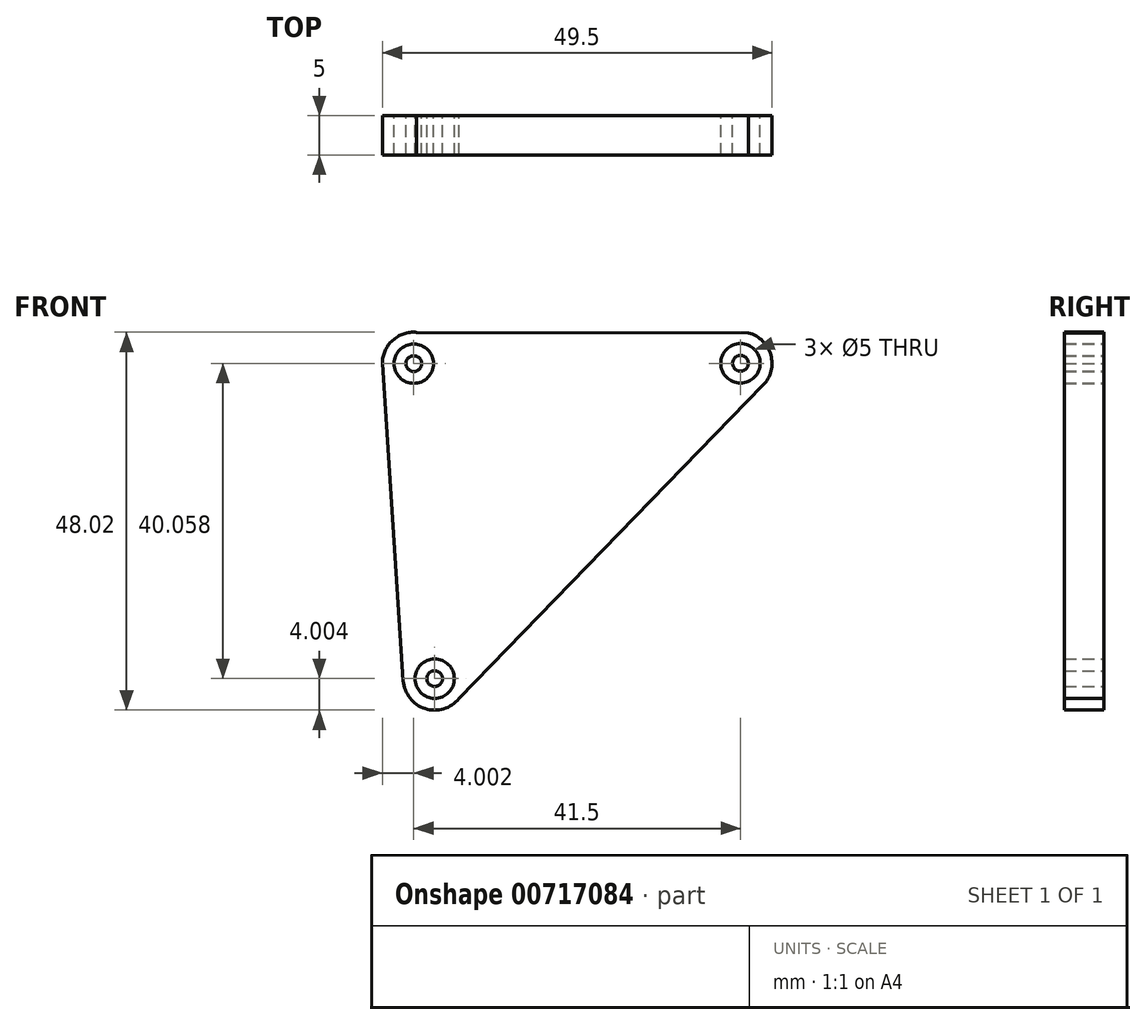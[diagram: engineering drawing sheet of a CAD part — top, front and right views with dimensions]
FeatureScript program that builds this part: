
annotation { "Feature Type Name" : "Feature", "Feature Type Description" : "" }
export const myFeature = defineFeature(function(context is Context, id is Id, definition is map)
    precondition{}
    {
        {
            var Q0;
            Q0=qCreatedBy(makeId("Front.planeOp"),FACE);
            var sketch = newSketch(context, id + "F0", { "sketchPlane" : qUnion([Q0])});
            skCircle(sketch, "E0", {"center": v(-13.99, 13.26) * mm, "radius": 2.5 * mm});
            skCircle(sketch, "E1", {"center": v(27.51, 13.3) * mm, "radius": 2.5 * mm});
            skCircle(sketch, "E2", {"center": v(-11.33, -26.76) * mm, "radius": 2.5 * mm});
            skArc(sketch, "E3", {"start": v(-13.65, 17.24) * mm, "mid": v(-16.9, 16) * mm, "end": v(-17.95, 12.7) * mm});
            skArc(sketch, "E4", {"start": v(30.38, 10.52) * mm, "mid": v(30.96, 15.32) * mm, "end": v(26.48, 17.17) * mm});
            skArc(sketch, "E5", {"start": v(-15.32, -27.02) * mm, "mid": v(-12.55, -30.57) * mm, "end": v(-8.24, -29.29) * mm});
            skLineSegment(sketch, "E6", {"start": v(-13.65, 17.24) * mm, "end": v(28.56, 17.16) * mm});
            skLineSegment(sketch, "E7", {"start": v(-17.99, 13.29) * mm, "end": v(-15.32, -27.02) * mm});
            skLineSegment(sketch, "E8", {"start": v(-8.24, -29.29) * mm, "end": v(30.38, 10.52) * mm});
            skCircle(sketch, "E9", {"center": v(-13.99, 13.26) * mm, "radius": 1 * mm});
            skCircle(sketch, "E10", {"center": v(-11.33, -26.76) * mm, "radius": 1 * mm});
            skCircle(sketch, "E11", {"center": v(27.51, 13.3) * mm, "radius": 1 * mm});
            skSolve(sketch);
        }
        {
            var Q0;
            Q0=makeQuery(id+"F0.imprint","IMPRINT",FACE,{"disambiguationData":[TD([[makeQuery(id+"F0.imprint","IMPRINT",EDGE,{"derivedFrom":sQuery(id+"F0.wireOp",EDGE,"E0")}),-1.0]])]});
            extrude(context, id + "F1", {"entities" : qUnion([Q0]), "depth" : 5 * mm, "offsetDistance" : 25.4 * mm});
        }
        {
            var Q0;
            Q0=makeQuery(id+"F0.imprint","IMPRINT",FACE,{"disambiguationData":[TD([[makeQuery(id+"F0.imprint","IMPRINT",EDGE,{"derivedFrom":sQuery(id+"F0.wireOp",EDGE,"E9")}),1.0]])]});
            var Q1;
            Q1=makeQuery(id+"F0.imprint","IMPRINT",FACE,{"disambiguationData":[TD([[makeQuery(id+"F0.imprint","IMPRINT",EDGE,{"derivedFrom":sQuery(id+"F0.wireOp",EDGE,"E11")}),1.0]])]});
            var Q2;
            Q2=makeQuery(id+"F0.imprint","IMPRINT",FACE,{"disambiguationData":[TD([[makeQuery(id+"F0.imprint","IMPRINT",EDGE,{"derivedFrom":sQuery(id+"F0.wireOp",EDGE,"E10")}),1.0]])]});
            extrude(context, id + "F2", {"entities" : qUnion([Q0, Q1, Q2]), "depth" : 5 * mm, "offsetDistance" : 25.4 * mm});
        }
    });
